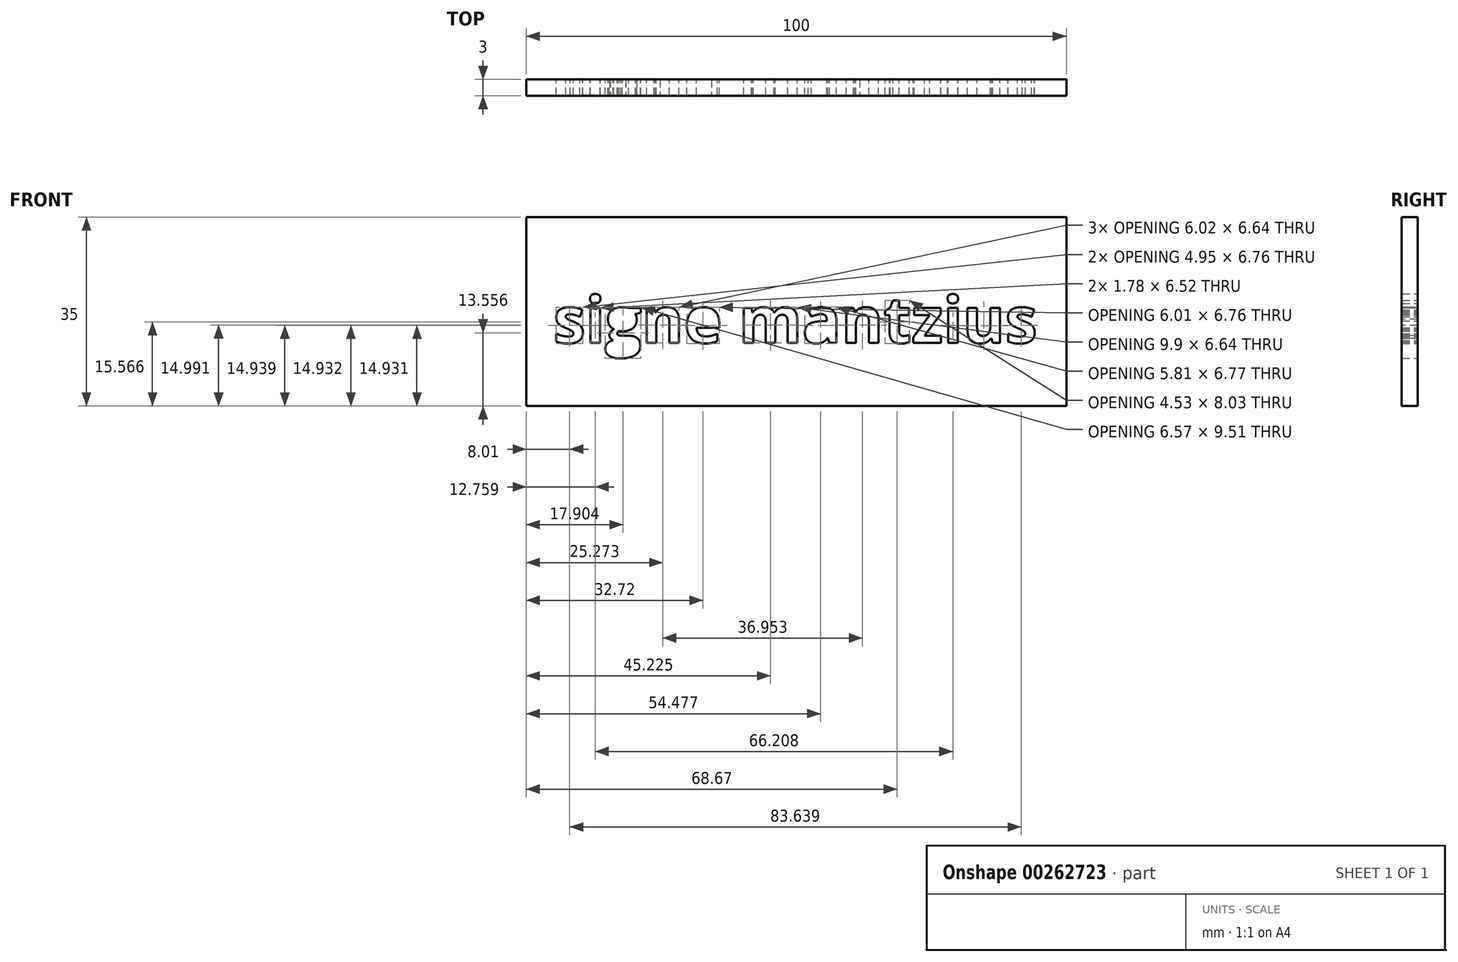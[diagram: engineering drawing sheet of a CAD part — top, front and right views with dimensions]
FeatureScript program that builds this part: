
annotation { "Feature Type Name" : "Feature", "Feature Type Description" : "" }
export const myFeature = defineFeature(function(context is Context, id is Id, definition is map)
    precondition{}
    {
        {
            var Q0;
            Q0=qCreatedBy(makeId("Front.planeOp"),FACE);
            var sketch = newSketch(context, id + "F0", { "sketchPlane" : qUnion([Q0])});
            skLineSegment(sketch, "E0.bottom", {"start": v(-154.93, -12.6) * mm, "end": v(-54.93, -12.6) * mm});
            skLineSegment(sketch, "E0.top", {"start": v(-154.93, -47.6) * mm, "end": v(-54.93, -47.6) * mm});
            skLineSegment(sketch, "E0.left", {"start": v(-154.93, -12.6) * mm, "end": v(-154.93, -47.6) * mm});
            skLineSegment(sketch, "E0.right", {"start": v(-54.93, -12.6) * mm, "end": v(-54.93, -47.6) * mm});
            skArc(sketch, "E1", {"start": v(-134.93, -12.6) * mm, "mid": v(-104.93, 17.4) * mm, "end": v(-74.93, -12.6) * mm});
            skCircle(sketch, "E2", {"center": v(-104.93, 11.4) * mm, "radius": 1.5 * mm});
            skText(sketch, "E3", { "text": "signe mantzius", "fontName": "OpenSans-Bold.ttf"});
            const initialGuessF0  = {"E3": [-0.14993, -0.03594, 1, 0, 0.0086]};
            skSetInitialGuess(sketch, initialGuessF0);
            skSolve(sketch);
        }
        {
            var Q0;
            Q0=makeQuery(id+"F0.imprint","IMPRINT",FACE,{"disambiguationData":[TD([[makeQuery(id+"F0.imprint","IMPRINT",EDGE,{"derivedFrom":sQuery(id+"F0.wireOp",EDGE,"E0.top")}),1.0]])]});
            var Q1;
            {var subQ0=sQuery(id+"F0.wireOp",EDGE,"E1");Q1=makeQuery(id+"F0.imprint","IMPRINT",FACE,{"disambiguationData":[TD([[makeQuery(id+"F0.imprint","IMPRINT",EDGE,{"derivedFrom":subQ0}),-1.0]])]});}
            extrude(context, id + "F1", {"entities" : qUnion([Q0, Q1]), "depth" : 3 * mm});
        }
    });
